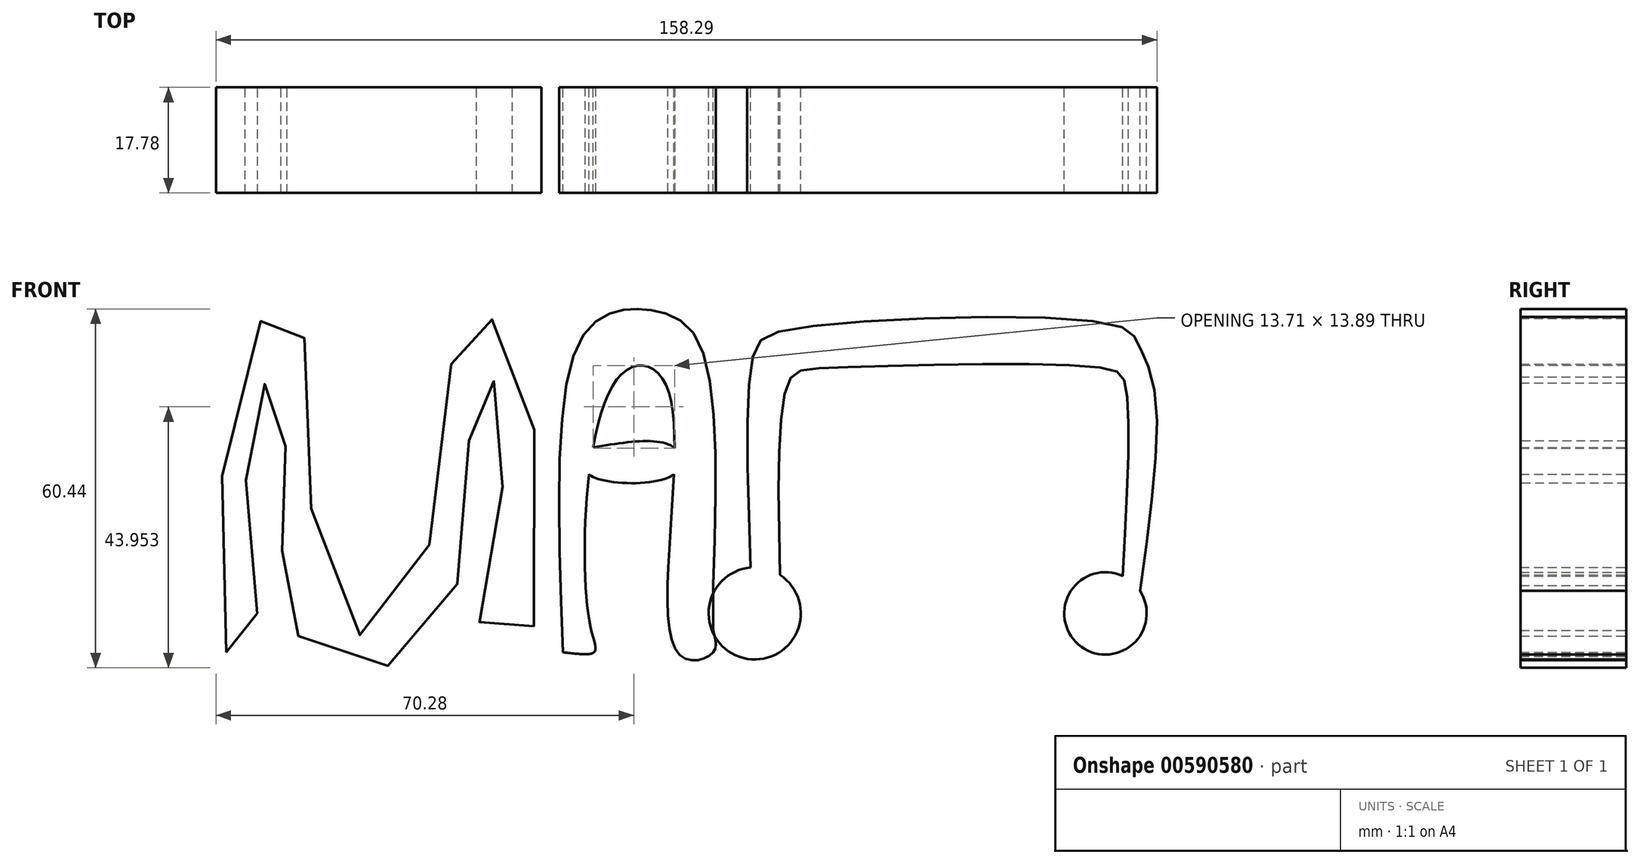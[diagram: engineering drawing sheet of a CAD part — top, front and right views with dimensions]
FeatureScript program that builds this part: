
annotation { "Feature Type Name" : "Feature", "Feature Type Description" : "" }
export const myFeature = defineFeature(function(context is Context, id is Id, definition is map)
    precondition{}
    {
        {
            var Q0;
            Q0=qCreatedBy(makeId("Front.planeOp"),FACE);
            var sketch = newSketch(context, id + "F0", { "sketchPlane" : qUnion([Q0])});
            skCircle(sketch, "E0", {"center": v(16.91, 6.56) * mm, "radius": 7.75 * mm});
            skCircle(sketch, "E1", {"center": v(75.92, 6.56) * mm, "radius": 6.94 * mm});
            skFitSpline(sketch, "E2", {"points": [v(21.17, 13.04) * mm, v(22.63, 45.55) * mm, v(29.13, 47.89) * mm, v(75.66, 47.89) * mm, v(79.3, 45.03) * mm, v(78.8, 12.86) * mm], "startDerivative": vector(-3.97, 168.84) * mm, "endDerivative": vector(-9.16, -165.49) * mm});
            skFitSpline(sketch, "E3", {"points": [v(16.25, 13.98) * mm, v(16.65, 49.97) * mm, v(22.9, 54.39) * mm, v(77.48, 55.17) * mm, v(81.38, 52.05) * mm, v(84.24, 43.73) * mm, v(81.72, 10.36) * mm], "startDerivative": vector(-7.15, 199.74) * mm, "endDerivative": vector(-25.11, -180.4) * mm});
            skSolve(sketch);
        }
        {
            var Q0;
            Q0=qCreatedBy(makeId("Front.planeOp"),FACE);
            var sketch = newSketch(context, id + "F1", { "sketchPlane" : qUnion([Q0])});
            skFitSpline(sketch, "E4", {"points": [v(-71.98, 0) * mm, v(-67.3, 54.39) * mm, v(-63.15, 56.2) * mm, v(-59.25, 54.13) * mm, v(-54.3, 6.82) * mm, v(-42.1, 6.3) * mm, v(-33, 53.09) * mm, v(-28.84, 56.2) * mm, v(-23.38, 51.79) * mm, v(-22.34, 0) * mm, v(-29.62, 6.04) * mm, v(-23.9, 38.53) * mm, v(-28.84, 46.33) * mm, v(-31.43, 27.1) * mm, v(-39.5, 0) * mm, v(-57.43, 0) * mm, v(-62.1, 11.76) * mm, v(-62.63, 27.35) * mm, v(-62.89, 44.5) * mm, v(-66.79, 44.25) * mm, v(-67.83, 18.52) * mm, v(-68.09, 0) * mm, v(-71.98, 0) * mm]});
            skFitSpline(sketch, "E5", {"points": [v(-15.32, 0) * mm, v(-12.72, 52.05) * mm, v(-5.96, 57.5) * mm, v(0, 57.5) * mm, v(7.04, 53.09) * mm, v(9.9, 11.24) * mm], "startDerivative": vector(-7.65, 198.07) * mm, "endDerivative": vector(-6.27, -178.22) * mm});
            skFitSpline(sketch, "E6", {"points": [v(9.9, 3.7) * mm, v(9.9, 0) * mm, v(3.92, 0) * mm, v(2.1, 44.77) * mm, v(-5.96, 46.33) * mm, v(-10.9, 5.26) * mm, v(-10.12, 0) * mm, v(-15.32, 0) * mm], "startDerivative": vector(16.84, -51.61) * mm, "endDerivative": vector(-73.9, 8.79) * mm});
            skFitSpline(sketch, "E7", {"points": [v(-13.07, -0.27) * mm, v(-15.32, 0) * mm, v(-10.12, 0) * mm], "startDerivative": vector(-8.5, 0.8) * mm, "endDerivative": vector(12.94, -0.2) * mm});
            skFitSpline(sketch, "E8", {"points": [v(-10.29, 34.5) * mm, v(3.43, 34.4) * mm, v(3.32, 29.96) * mm, v(-10.95, 29.96) * mm, v(-10.6, 32.58) * mm], "startDerivative": vector(51.65, 8.55) * mm, "endDerivative": vector(12.05, 19.58) * mm});
            skFitSpline(sketch, "E9", {"points": [v(9.9, 11.24) * mm, v(9.9, 3.7) * mm], "startDerivative": vector(0, -7.54) * mm, "endDerivative": vector(0, -7.54) * mm});
            skSolve(sketch);
        }
        {
            var Q0;
            Q0 = qSketchRegion(id + "F1", true);
            var Q1;
            Q1 = qSketchRegion(id + "F0", true);
            extrude(context, id + "F2", {"entities" : qUnion([Q0, Q1]), "depth" : 17.78 * mm, "offsetDistance" : 25.4 * mm});
        }
    });
